# Revit family: ROTHOB_Rothoblaas_Plate_Alumini
name_source: partatom
category: Structural Connections
units: mm (PartAtom-declared; Revit-internal decimal feet)

## family parameters
Cut with Voids When Loaded = No
Enable cutting in views = Yes
Host = Face
Material for Model Behavior = Other
OmniClass Number = 23.13.23.11.19.13
OmniClass Title = Wood Connectors
Shared = No

## types (6) — shared parameters
BIMObjectName = ROTHOB_Rothoblaas_Plate_Alumini
CECode = ETA-09/0361
Category = Pr_20_76_51_07: Aluminium structural sections
CodePerformance = CE - Construction products
Color = Silver
Default Elevation = 1219.2 mm  [stored 4 ft]
Description = Concealed bracket without holes
DurationUnit = Years
Esporta tipo in formato IFC con nome = IfcMemberType
ExpectedLife = 50
Features = Bracket for timber-to-timber, timber-to-concrete, timber-to-steel joints
IfcExportAs = IfcMemberType
IfcExportType = USERDEFINED
ManufacturerName = ROTHO BLAAS SRL
ManufacturerURL = www.rothoblaas.com
Material = Aluminium
ModelDisclaimer = The latest version of the data sheets can be found on our website
Name = Plate
NominalLength = 109.9 mm  [stored 0.360564 ft]
NominalWidth = 45 mm  [stored 0.147638 ft]
ObjectMaterial = ROTHOB_Rothoblaas_Aluminium
OmniClassCode = 23-13 23 11 19 13
OmniClassTitle = Wood Connectors
OmniClassVersion = 2012-05-16
ProductInformation = https://www.rothoblaas.com
Revision = 1
Shape = Three-dimensional
Thickness_s = 6 mm  [stored 0.019685 ft]
Tipo IFC predefinito = USERDEFINED
UniClass2015Code = Pr_20_76_51_07
UniClass2015Title = Aluminium structural sections
UniClass2015Version = Products v1.33
Version = 2
WebLength_LB = 109.9 mm  [stored 0.360564 ft]
WingWidth_LA = 45 mm  [stored 0.147638 ft]

## per-type parameters (varying)
| type | HasHole_ALUMINI125 | HasHole_ALUMINI155 | HasHole_ALUMINI185 | HasHole_ALUMINI215 | HasHole_ALUMINI65 | HasHole_ALUMINI95 | Height_H | MinWeight | ModelNumber | NominalHeight | Size |
| ALUMINI65_065x45x109.90mm | No | No | No | No | Yes | No | 65 mm  [stored 0.213255 ft] | 0.149 kg | ALUMINI65 | 65 mm  [stored 0.213255 ft] | 65x45x109.90 mm |
| ALUMINI95_095x45x109.90mm | No | No | No | No | No | Yes | 95 mm | 0.214 kg | ALUMINI95 | 95 mm | 95x45x109.90 mm |
| ALUMINI125_125x45x109.90mm | Yes | No | No | No | No | No | 125 mm | 0.286 kg | ALUMINI125 | 125 mm | 125x45x109.90 mm |
| ALUMINI155_155x45x109.90mm | No | Yes | No | No | No | No | 155 mm | 0.350 kg | ALUMINI155 | 155 mm | 155x45x109.90 mm |
| ALUMINI185_185x45x109.90mm | No | No | Yes | No | No | No | 185 mm  [stored 0.606955 ft] | 0.416 kg | ALUMINI185 | 185 mm  [stored 0.606955 ft] | 185x45x109.90 mm |
| ALUMINI215_215x45x109.90mm | No | No | No | Yes | No | No | 215 mm | 0.416 kg | ALUMINI215 | 215 mm | 215x45x109.90 mm |

note: [stored X ft] marks values corroborated as IEEE doubles in the binary element streams (Revit-internal decimal feet)
